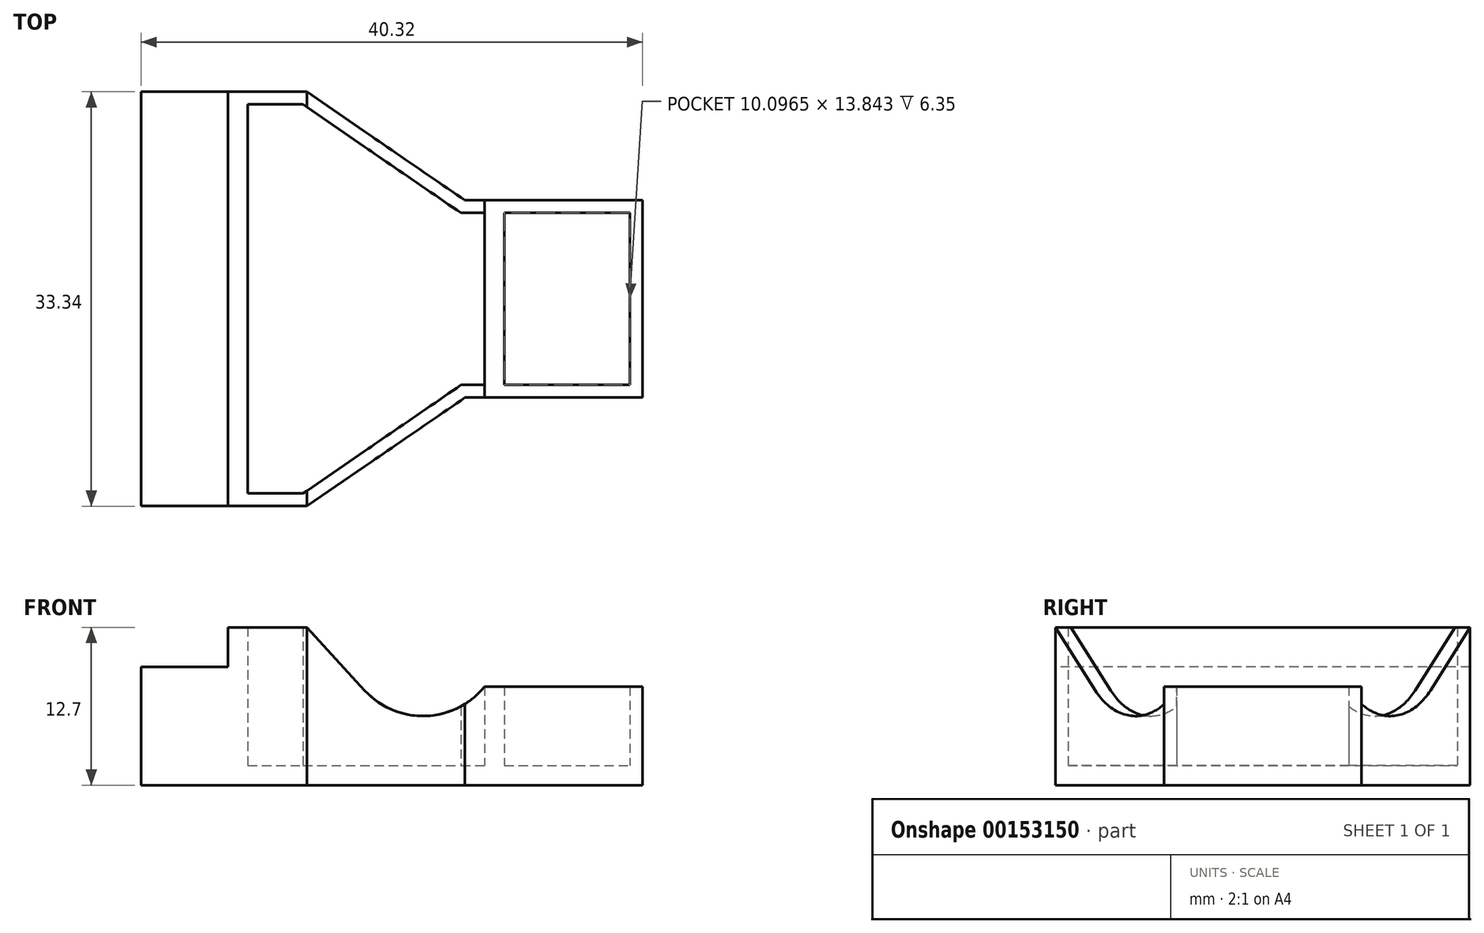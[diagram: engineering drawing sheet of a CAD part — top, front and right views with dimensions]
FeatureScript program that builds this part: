
annotation { "Feature Type Name" : "Feature", "Feature Type Description" : "" }
export const myFeature = defineFeature(function(context is Context, id is Id, definition is map)
    precondition{}
    {
        {
            var Q0;
            Q0=qCreatedBy(makeId("Front.planeOp"),FACE);
            var sketch = newSketch(context, id + "F0", { "sketchPlane" : qUnion([Q0])});
            skLineSegment(sketch, "E0", {"start": v(-7.94, 33.34) * mm, "end": v(7.94, 33.34) * mm});
            skLineSegment(sketch, "E1", {"start": v(7.94, 33.34) * mm, "end": v(7.94, 19.05) * mm});
            skLineSegment(sketch, "E2", {"start": v(7.94, 19.05) * mm, "end": v(16.67, 6.35) * mm});
            skLineSegment(sketch, "E3", {"start": v(16.67, 6.35) * mm, "end": v(16.67, 0) * mm});
            skLineSegment(sketch, "E4", {"start": v(16.67, 0) * mm, "end": v(-16.67, 0) * mm});
            skLineSegment(sketch, "E5", {"start": v(-16.67, 0) * mm, "end": v(-16.67, 6.35) * mm});
            skLineSegment(sketch, "E6", {"start": v(-16.67, 6.35) * mm, "end": v(-7.94, 19.05) * mm});
            skLineSegment(sketch, "E7", {"start": v(-7.94, 19.05) * mm, "end": v(-7.94, 33.34) * mm});
            skLineSegment(sketch, "E8.2", {"start": v(15.65, 1.59) * mm, "end": v(-15.65, 1.59) * mm});
            skLineSegment(sketch, "E9", {"start": v(-6.92, 20.64) * mm, "end": v(6.92, 20.64) * mm});
            skLineSegment(sketch, "E10", {"start": v(-6.92, 22.22) * mm, "end": v(6.92, 22.23) * mm});
            skLineSegment(sketch, "E11.0", {"start": v(6.92, 32.32) * mm, "end": v(6.92, 22.23) * mm});
            skLineSegment(sketch, "E12.0", {"start": v(-6.92, 18.73) * mm, "end": v(-6.92, 20.64) * mm});
            skLineSegment(sketch, "E13.0", {"start": v(-15.65, 6.03) * mm, "end": v(-6.92, 18.73) * mm});
            skLineSegment(sketch, "E14.0", {"start": v(6.92, 18.73) * mm, "end": v(15.65, 6.03) * mm});
            skLineSegment(sketch, "E15.0", {"start": v(15.65, 6.03) * mm, "end": v(15.65, 1.59) * mm});
            skLineSegment(sketch, "E16.0", {"start": v(-15.65, 1.59) * mm, "end": v(-15.65, 6.03) * mm});
            skLineSegment(sketch, "E17.trimOffspring", {"start": v(6.92, 20.64) * mm, "end": v(6.92, 18.73) * mm});
            skLineSegment(sketch, "E18.trimOffspring", {"start": v(-6.92, 22.22) * mm, "end": v(-6.92, 32.32) * mm});
            skLineSegment(sketch, "E19.0", {"start": v(-6.92, 32.32) * mm, "end": v(6.92, 32.32) * mm});
            skSolve(sketch);
        }
        {
            var Q0;
            Q0=qSketchRegion(id+"F0",true);
            extrude(context, id + "F1", {"entities" : qUnion([Q0]), "depth" : 12.7 * mm});
        }
        {
            var Q0;
            Q0=qCreatedBy(makeId("Front.planeOp"),FACE);
            var sketch = newSketch(context, id + "F2", { "sketchPlane" : qUnion([Q0])});
            skLineSegment(sketch, "E20.0", {"start": v(-7.94, 33.34) * mm, "end": v(7.94, 33.34) * mm});
            skLineSegment(sketch, "E21.0", {"start": v(7.94, 33.34) * mm, "end": v(7.94, 19.05) * mm});
            skLineSegment(sketch, "E22.0", {"start": v(7.94, 19.05) * mm, "end": v(16.67, 6.35) * mm});
            skLineSegment(sketch, "E23.0", {"start": v(16.67, 6.35) * mm, "end": v(16.67, 0) * mm});
            skLineSegment(sketch, "E24.0", {"start": v(16.67, 0) * mm, "end": v(-16.67, 0) * mm});
            skLineSegment(sketch, "E25.0", {"start": v(-16.67, 0) * mm, "end": v(-16.67, 6.35) * mm});
            skLineSegment(sketch, "E26.0", {"start": v(-16.67, 6.35) * mm, "end": v(-7.94, 19.05) * mm});
            skLineSegment(sketch, "E27.0", {"start": v(-7.94, 19.05) * mm, "end": v(-7.94, 33.34) * mm});
            skSolve(sketch);
        }
        {
            var Q0;
            Q0=qSketchRegion(id+"F2",true);
            extrude(context, id + "F3", {"entities" : qUnion([Q0]), "operationType" : NewBodyOperationType.ADD, "depth" : 1.59 * mm});
        }
        {
            var Q0;
            Q0=makeQuery(id+"F1.opExtrude","SWEPT_FACE",FACE,{"disambiguationData":[OSD([sQuery(id+"F0.wireOp",EDGE,"E3")])]});
            var sketch = newSketch(context, id + "F4", { "sketchPlane" : qUnion([Q0])});
            skLineSegment(sketch, "E28", {"start": v(-12.7, 6.35) * mm, "end": v(-7.62, 11) * mm});
            skLineSegment(sketch, "E29", {"start": v(-7.94, 33.34) * mm, "end": v(-7.94, 20.64) * mm});
            skLineSegment(sketch, "E30", {"start": v(-5.56, 28.09) * mm, "end": v(-5.56, 3.28) * mm, "construction": true});
            skArc(sketch, "E31", {"start": v(-7.62, 11) * mm, "mid": v(-5.56, 15.89) * mm, "end": v(-7.94, 20.64) * mm});
            skLineSegment(sketch, "E32", {"start": v(-7.94, 33.34) * mm, "end": v(-12.7, 33.34) * mm});
            skLineSegment(sketch, "E33", {"start": v(-12.7, 33.34) * mm, "end": v(-12.7, 6.35) * mm});
            skSolve(sketch);
        }
        {
            var Q0;
            Q0=qSketchRegion(id+"F4",true);
            extrude(context, id + "F5", {"entities" : qUnion([Q0]), "operationType" : NewBodyOperationType.REMOVE, "endBound" : BoundingType.THROUGH_ALL, "oppositeDirection" : true, "depth" : 25.4 * mm});
        }
        {
            var Q0;
            Q0=makeQuery(id+"F1.opExtrude","SWEPT_FACE",FACE,{"disambiguationData":[OSD([sQuery(id+"F0.wireOp",EDGE,"E4")])]});
            var sketch = newSketch(context, id + "F6", { "sketchPlane" : qUnion([Q0])});
            skLineSegment(sketch, "E34.bottom", {"start": v(-16.67, 0) * mm, "end": v(16.67, 0) * mm});
            skLineSegment(sketch, "E34.top", {"start": v(-16.67, 9.52) * mm, "end": v(16.67, 9.52) * mm});
            skLineSegment(sketch, "E34.left", {"start": v(-16.67, 0) * mm, "end": v(-16.67, 9.52) * mm});
            skLineSegment(sketch, "E34.right", {"start": v(16.67, 0) * mm, "end": v(16.67, 9.52) * mm});
            skSolve(sketch);
        }
        {
            var Q0;
            Q0=qSketchRegion(id+"F6",true);
            extrude(context, id + "F7", {"entities" : qUnion([Q0]), "operationType" : NewBodyOperationType.ADD, "depth" : 7 * mm});
        }
        {
            var Q0;
            Q0=makeQuery(id+"F7.opExtrude","CAP_FACE",FACE,{"disambiguationData":[OSD([sQuery(id+"F6.wireOp",EDGE,"E34.bottom"),sQuery(id+"F6.wireOp",EDGE,"E34.top"),sQuery(id+"F6.wireOp",EDGE,"E34.left"),sQuery(id+"F6.wireOp",EDGE,"E34.right")])],"isStart":false});
            var sketch = newSketch(context, id + "F8", { "sketchPlane" : qUnion([Q0])});
            skLineSegment(sketch, "E35.bottom", {"start": v(-16.67, 0) * mm, "end": v(16.67, 0) * mm});
            skLineSegment(sketch, "E35.top", {"start": v(-16.67, 12.7) * mm, "end": v(16.67, 12.7) * mm});
            skLineSegment(sketch, "E35.left", {"start": v(-16.67, 0) * mm, "end": v(-16.67, 12.7) * mm});
            skLineSegment(sketch, "E35.right", {"start": v(16.67, 0) * mm, "end": v(16.67, 12.7) * mm});
            skSolve(sketch);
        }
        {
            var Q0;
            Q0=makeQuery(id+"F1.opExtrude","SWEPT_BODY",BODY,{"disambiguationData":[OSD([sQuery(id+"F0.wireOp",EDGE,"E0"),sQuery(id+"F0.wireOp",EDGE,"E1"),sQuery(id+"F0.wireOp",EDGE,"E2"),sQuery(id+"F0.wireOp",EDGE,"E3"),sQuery(id+"F0.wireOp",EDGE,"E4"),sQuery(id+"F0.wireOp",EDGE,"E5"),sQuery(id+"F0.wireOp",EDGE,"E6"),sQuery(id+"F0.wireOp",EDGE,"E7"),sQuery(id+"F0.wireOp",EDGE,"E8.0"),sQuery(id+"F0.wireOp",EDGE,"E8.1"),sQuery(id+"F0.wireOp",EDGE,"E8.2"),sQuery(id+"F0.wireOp",EDGE,"E8.3"),sQuery(id+"F0.wireOp",EDGE,"E8.4"),sQuery(id+"F0.wireOp",EDGE,"E8.5"),sQuery(id+"F0.wireOp",EDGE,"E8.6"),sQuery(id+"F0.wireOp",EDGE,"E8.7"),sQuery(id+"F0.wireOp",EDGE,"E9"),sQuery(id+"F0.wireOp",EDGE,"E10"),sQuery(id+"F0.wireOp",EDGE,"ed1682e8-f494-45ca-96d8-cc6ea4883137.trimOffspring"),sQuery(id+"F0.wireOp",EDGE,"4fed57be-da0a-41fb-ba59-8bc84a799902.trimOffspring")])]});
            var Q1;
            Q1=sQuery(id+"F8.wireOp",EDGE,"E35.bottom");
            transform(context, id + "F9", {"entities" : qUnion([Q0]), "transformType" : TransformType.ROTATION, "transformAxis" : qUnion([Q1]), "angle" : 90 * degree, "oppositeDirection" : true, "makeCopy" : false});
        }
        {
            var Q0;
            Q0=makeQuery(id+"F7.opExtrude","CAP_FACE",FACE,{"disambiguationData":[OSD([sQuery(id+"F6.wireOp",EDGE,"E34.bottom"),sQuery(id+"F6.wireOp",EDGE,"E34.top"),sQuery(id+"F6.wireOp",EDGE,"E34.left"),sQuery(id+"F6.wireOp",EDGE,"E34.right")])],"isStart":false});
            var sketch = newSketch(context, id + "F10", { "sketchPlane" : qUnion([Q0])});
            skLineSegment(sketch, "E36", {"start": v(0, -6.99) * mm, "end": v(0, 2.54) * mm, "construction": true});
            skSolve(sketch);
        }
        {
            var Q0;
            Q0=makeQuery(id+"F1.opExtrude","SWEPT_BODY",BODY,{"disambiguationData":[OSD([sQuery(id+"F0.wireOp",EDGE,"E0"),sQuery(id+"F0.wireOp",EDGE,"E1"),sQuery(id+"F0.wireOp",EDGE,"E2"),sQuery(id+"F0.wireOp",EDGE,"E3"),sQuery(id+"F0.wireOp",EDGE,"E4"),sQuery(id+"F0.wireOp",EDGE,"E5"),sQuery(id+"F0.wireOp",EDGE,"E6"),sQuery(id+"F0.wireOp",EDGE,"E7"),sQuery(id+"F0.wireOp",EDGE,"E8.0"),sQuery(id+"F0.wireOp",EDGE,"E8.1"),sQuery(id+"F0.wireOp",EDGE,"E8.2"),sQuery(id+"F0.wireOp",EDGE,"E8.3"),sQuery(id+"F0.wireOp",EDGE,"E8.4"),sQuery(id+"F0.wireOp",EDGE,"E8.5"),sQuery(id+"F0.wireOp",EDGE,"E8.6"),sQuery(id+"F0.wireOp",EDGE,"E8.7"),sQuery(id+"F0.wireOp",EDGE,"E9"),sQuery(id+"F0.wireOp",EDGE,"E10"),sQuery(id+"F0.wireOp",EDGE,"ed1682e8-f494-45ca-96d8-cc6ea4883137.trimOffspring"),sQuery(id+"F0.wireOp",EDGE,"4fed57be-da0a-41fb-ba59-8bc84a799902.trimOffspring")])]});
            var Q1;
            Q1=sQuery(id+"F10.wireOp",EDGE,"E36");
            transform(context, id + "F11", {"entities" : qUnion([Q0]), "transformType" : TransformType.ROTATION, "transformAxis" : qUnion([Q1]), "angle" : 90 * degree, "oppositeDirection" : true, "makeCopy" : false});
        }
        {
            var Q0;
            Q0=makeQuery(id+"F1.opExtrude","SWEPT_BODY",BODY,{"disambiguationData":[OSD([sQuery(id+"F0.wireOp",EDGE,"E0"),sQuery(id+"F0.wireOp",EDGE,"E1"),sQuery(id+"F0.wireOp",EDGE,"E2"),sQuery(id+"F0.wireOp",EDGE,"E3"),sQuery(id+"F0.wireOp",EDGE,"E4"),sQuery(id+"F0.wireOp",EDGE,"E5"),sQuery(id+"F0.wireOp",EDGE,"E6"),sQuery(id+"F0.wireOp",EDGE,"E7"),sQuery(id+"F0.wireOp",EDGE,"E8.0"),sQuery(id+"F0.wireOp",EDGE,"E8.1"),sQuery(id+"F0.wireOp",EDGE,"E8.2"),sQuery(id+"F0.wireOp",EDGE,"E8.3"),sQuery(id+"F0.wireOp",EDGE,"E8.4"),sQuery(id+"F0.wireOp",EDGE,"E8.5"),sQuery(id+"F0.wireOp",EDGE,"E8.6"),sQuery(id+"F0.wireOp",EDGE,"E8.7"),sQuery(id+"F0.wireOp",EDGE,"E9"),sQuery(id+"F0.wireOp",EDGE,"E10"),sQuery(id+"F0.wireOp",EDGE,"ed1682e8-f494-45ca-96d8-cc6ea4883137.trimOffspring"),sQuery(id+"F0.wireOp",EDGE,"4fed57be-da0a-41fb-ba59-8bc84a799902.trimOffspring")])]});
            var Q1;
            Q1=makeQuery(id+"F1.opExtrude","SWEPT_EDGE",EDGE,{"disambiguationData":[OSD([sQuery(id+"F0.wireOp",EDGE,"E2"),sQuery(id+"F0.wireOp",EDGE,"E3")])]});
            transform(context, id + "F12", {"entities" : qUnion([Q0]), "transformType" : TransformType.TRANSLATION_DISTANCE, "transformDirection" : qUnion([Q1]), "distance" : 5.7 * mm, "makeCopy" : false});
        }
    });
